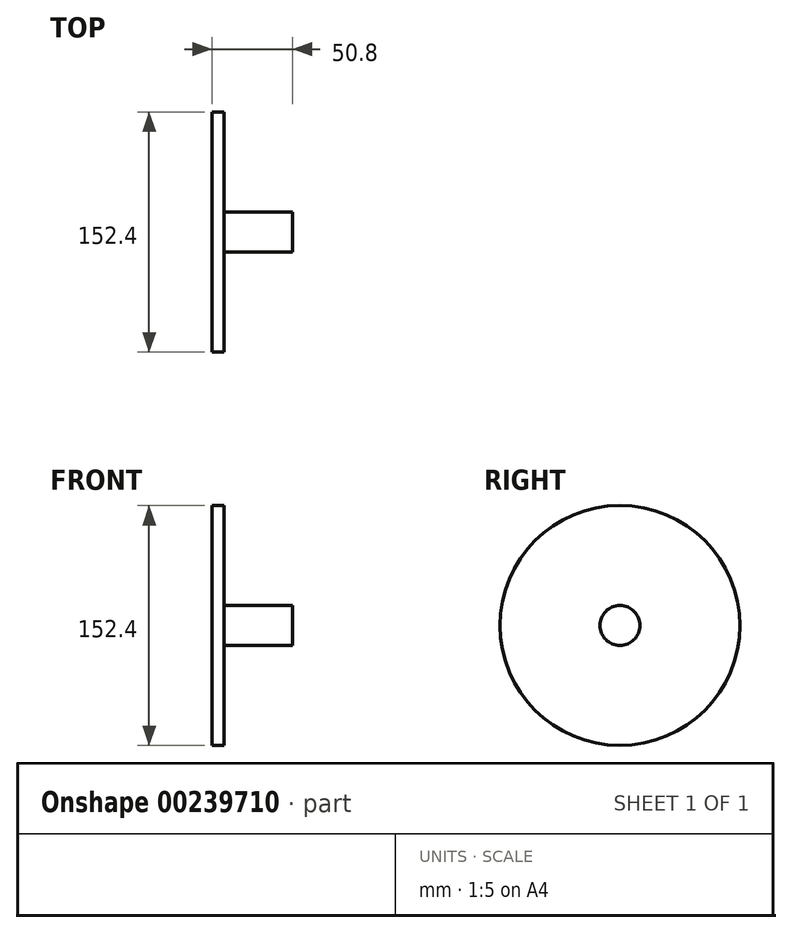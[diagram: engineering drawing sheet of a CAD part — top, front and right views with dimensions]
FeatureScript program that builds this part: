
annotation { "Feature Type Name" : "Feature", "Feature Type Description" : "" }
export const myFeature = defineFeature(function(context is Context, id is Id, definition is map)
    precondition{}
    {
        {
            var Q0;
            Q0=qCreatedBy(makeId("Front.planeOp"),FACE);
            var sketch = newSketch(context, id + "F0", { "sketchPlane" : qUnion([Q0])});
            skLineSegment(sketch, "E0", {"start": v(0, 0) * mm, "end": v(0, 76.2) * mm});
            skLineSegment(sketch, "E1", {"start": v(0, 76.2) * mm, "end": v(7.62, 76.2) * mm});
            skLineSegment(sketch, "E2", {"start": v(7.62, 76.2) * mm, "end": v(7.62, 12.7) * mm});
            skLineSegment(sketch, "E3", {"start": v(7.62, 12.7) * mm, "end": v(50.8, 12.7) * mm});
            skLineSegment(sketch, "E4", {"start": v(50.8, 12.7) * mm, "end": v(50.8, 0) * mm});
            skLineSegment(sketch, "E5", {"start": v(50.8, 0) * mm, "end": v(0, 0) * mm});
            skSolve(sketch);
        }
        {
            var Q0;
            Q0=makeQuery(id+"F0.imprint","IMPRINT",FACE,{"disambiguationData":[TD([[makeQuery(id+"F0.imprint","IMPRINT",EDGE,{"derivedFrom":sQuery(id+"F0.wireOp",EDGE,"E0")}),-1.0]])]});
            var Q1;
            Q1=sQuery(id+"F0.wireOp",EDGE,"E5");
            revolve(context, id + "F1", {"entities" : qUnion([Q0]), "axis" : qUnion([Q1]), "revolveType" : RevolveType.FULL});
        }
    });
